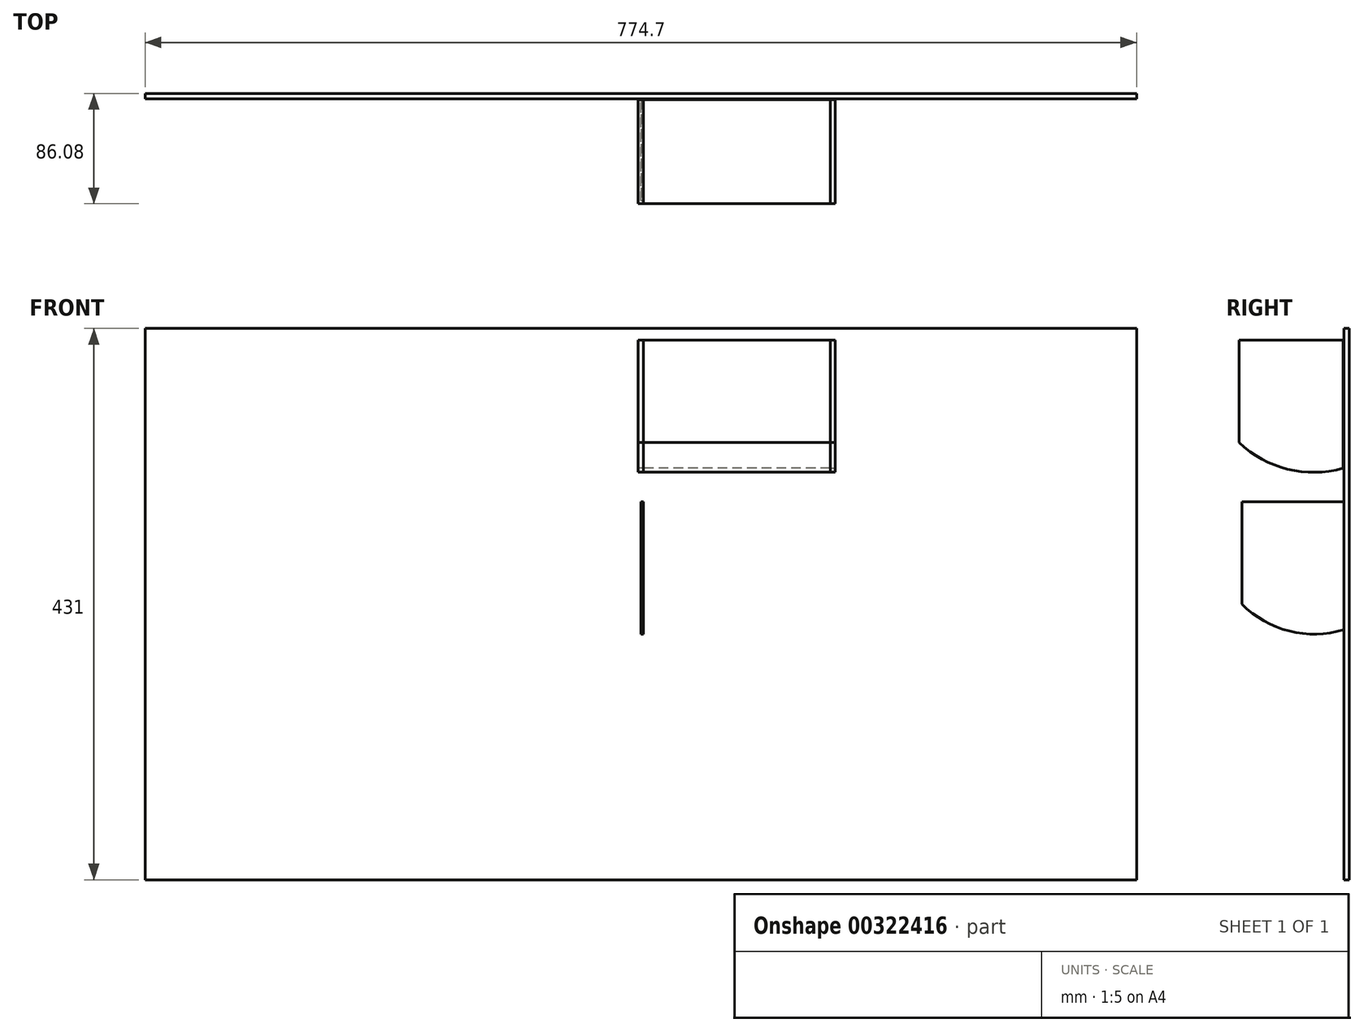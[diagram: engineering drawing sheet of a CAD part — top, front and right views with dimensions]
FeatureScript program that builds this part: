
annotation { "Feature Type Name" : "Feature", "Feature Type Description" : "" }
export const myFeature = defineFeature(function(context is Context, id is Id, definition is map)
    precondition{}
    {
        {
            var Q0;
            Q0=qCreatedBy(makeId("Front.planeOp"),FACE);
            var sketch = newSketch(context, id + "F0", { "sketchPlane" : qUnion([Q0])});
            skLineSegment(sketch, "E0.bottom", {"start": v(-387.35, 215.5) * mm, "end": v(387.35, 215.5) * mm});
            skLineSegment(sketch, "E0.top", {"start": v(-387.35, -215.5) * mm, "end": v(387.35, -215.5) * mm});
            skLineSegment(sketch, "E0.left", {"start": v(-387.35, 215.5) * mm, "end": v(-387.35, -215.5) * mm});
            skLineSegment(sketch, "E0.right", {"start": v(387.35, 215.5) * mm, "end": v(387.35, -215.5) * mm});
            skPoint(sketch, "E0.middle", {"position": v(0, 0) * mm});
            skSolve(sketch);
        }
        {
            var Q0;
            Q0 = qSketchRegion(id + "F0", true);
            extrude(context, id + "F1", {"entities" : qUnion([Q0]), "depth" : 4 * mm});
        }
        {
            var Q0;
            Q0=qCreatedBy(makeId("Right.planeOp"),FACE);
            var sketch = newSketch(context, id + "F2", { "sketchPlane" : qUnion([Q0])});
            skLineSegment(sketch, "E1", {"start": v(-4.79, 106.22) * mm, "end": v(-4.79, 206.22) * mm});
            skLineSegment(sketch, "E2", {"start": v(-4.79, 206.22) * mm, "end": v(-86.08, 206.22) * mm});
            skLineSegment(sketch, "E3", {"start": v(-86.08, 206.22) * mm, "end": v(-86.08, 126.22) * mm});
            skArc(sketch, "E4", {"start": v(-86.08, 126.22) * mm, "mid": v(-48.08, 105.46) * mm, "end": v(-4.79, 106.22) * mm});
            skSolve(sketch);
        }
        {
            var Q0;
            Q0=makeQuery(id+"F2.imprint","IMPRINT",FACE,{"disambiguationData":[TD([[makeQuery(id+"F2.imprint","IMPRINT",EDGE,{"derivedFrom":sQuery(id+"F2.wireOp",EDGE,"E1")}),1.0]])]});
            extrude(context, id + "F3", {"entities" : qUnion([Q0]), "depth" : 2 * mm, "hasSecondDirection" : true, "secondDirectionOppositeDirection" : true, "secondDirectionDepth" : 2 * mm});
        }
        {
            var Q0;
            Q0=qCreatedBy(makeId("Right.planeOp"),FACE);
            cPlane(context, id + "F4", {"entities" : qUnion([Q0]), "cplaneType" : CPlaneType.OFFSET, "offset" : (150 / 2) * mm, "width" : 150 * mm, "height" : 150 * mm});
        }
        {
            var Q0;
            Q0=makeQuery(id+"F3.opExtrude","SWEPT_BODY",BODY,{"disambiguationData":[OSD([sQuery(id+"F2.wireOp",EDGE,"E1"),sQuery(id+"F2.wireOp",EDGE,"E2"),sQuery(id+"F2.wireOp",EDGE,"E3"),sQuery(id+"F2.wireOp",EDGE,"E4")])]});
            var Q1;
            Q1=qCreatedBy(id+"F4.planeOp",FACE);
            mirror(context, id + "F5", {"entities" : qUnion([Q0]), "mirrorPlane" : qUnion([Q1])});
        }
        {
            var Q0;
            Q0=makeQuery(id+"F3.opExtrude","CAP_FACE",FACE,{"disambiguationData":[OSD([sQuery(id+"F2.wireOp",EDGE,"E1"),sQuery(id+"F2.wireOp",EDGE,"E2"),sQuery(id+"F2.wireOp",EDGE,"E3"),sQuery(id+"F2.wireOp",EDGE,"E4")])],"isStart":true});
            cPlane(context, id + "F6", {"entities" : qUnion([Q0]), "cplaneType" : CPlaneType.OFFSET, "offset" : 11 * mm, "width" : 150 * mm, "height" : 150 * mm});
        }
        {
            var Q0;
            Q0=makeQuery(id+"F3.opExtrude","CAP_FACE",FACE,{"disambiguationData":[OSD([sQuery(id+"F2.wireOp",EDGE,"E1"),sQuery(id+"F2.wireOp",EDGE,"E2"),sQuery(id+"F2.wireOp",EDGE,"E3"),sQuery(id+"F2.wireOp",EDGE,"E4")])],"isStart":false});
            extrude(context, id + "F7", {"entities" : qUnion([Q0]), "depth" : 146 * mm});
        }
        {
            var Q0;
            Q0=qCreatedBy(makeId("Right.planeOp"),FACE);
            var sketch = newSketch(context, id + "F8", { "sketchPlane" : qUnion([Q0])});
            skLineSegment(sketch, "E5", {"start": v(-3.89, -20) * mm, "end": v(-3.89, 80) * mm});
            skLineSegment(sketch, "E6", {"start": v(-3.89, 80) * mm, "end": v(-83.89, 80) * mm});
            skLineSegment(sketch, "E7", {"start": v(-83.89, 80) * mm, "end": v(-83.89, 0) * mm});
            skArc(sketch, "E8", {"start": v(-83.89, 0) * mm, "mid": v(-46.66, -21.1) * mm, "end": v(-3.89, -20) * mm});
            skSolve(sketch);
        }
        {
            var Q0;
            Q0=makeQuery(id+"F8.imprint","IMPRINT",FACE,{"disambiguationData":[TD([[makeQuery(id+"F8.imprint","IMPRINT",EDGE,{"derivedFrom":sQuery(id+"F8.wireOp",EDGE,"E5")}),1.0]])]});
            extrude(context, id + "F9", {"entities" : qUnion([Q0]), "operationType" : NewBodyOperationType.ADD, "depth" : 2 * mm});
        }
    });
